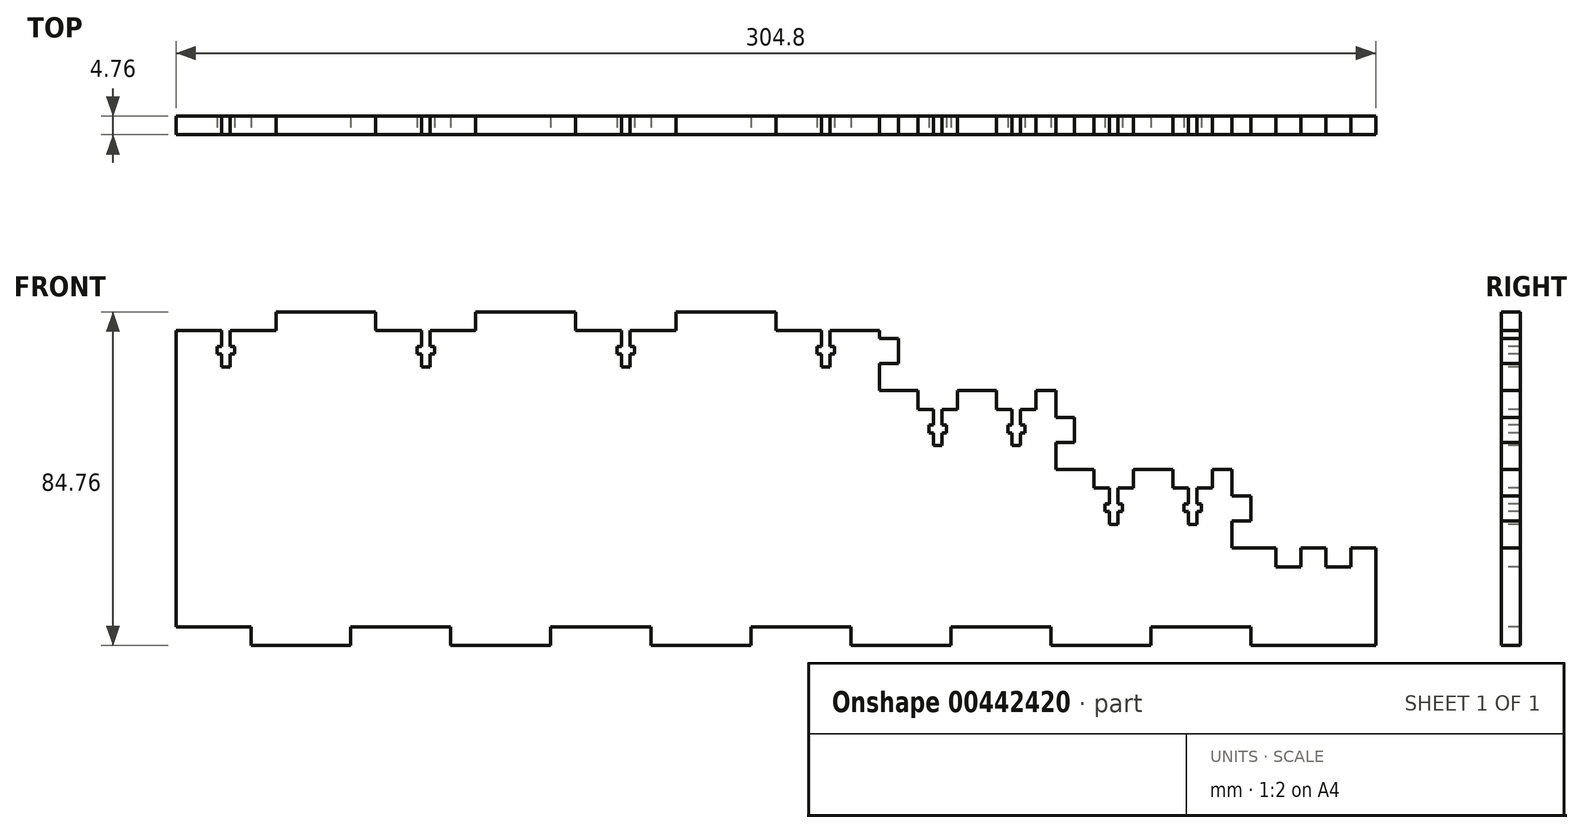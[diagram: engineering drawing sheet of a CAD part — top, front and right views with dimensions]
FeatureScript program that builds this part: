
annotation { "Feature Type Name" : "Feature", "Feature Type Description" : "" }
export const myFeature = defineFeature(function(context is Context, id is Id, definition is map)
    precondition{}
    {
        {
            var Q0;
            Q0=qCreatedBy(makeId("Front.planeOp"),FACE);
            var sketch = newSketch(context, id + "F0", { "sketchPlane" : qUnion([Q0])});
            skLineSegment(sketch, "E0", {"start": v(0, 0) * mm, "end": v(-273.05, 0) * mm});
            skLineSegment(sketch, "E1", {"start": v(0, 0) * mm, "end": v(0, 44.76) * mm});
            skLineSegment(sketch, "E2", {"start": v(0, 44.76) * mm, "end": v(-44.76, 44.76) * mm});
            skLineSegment(sketch, "E3", {"start": v(-44.76, 44.76) * mm, "end": v(-44.76, 64.76) * mm});
            skLineSegment(sketch, "E4", {"start": v(-44.76, 64.76) * mm, "end": v(-89.53, 64.76) * mm});
            skLineSegment(sketch, "E5", {"start": v(-89.53, 64.76) * mm, "end": v(-89.53, 84.76) * mm});
            skLineSegment(sketch, "E6", {"start": v(-89.53, 84.76) * mm, "end": v(-129.53, 84.76) * mm});
            skLineSegment(sketch, "E7", {"start": v(-129.53, 84.76) * mm, "end": v(-129.53, 84.76) * mm});
            skLineSegment(sketch, "E8", {"start": v(-273.05, 0) * mm, "end": v(-273.05, 84.76) * mm});
            skLineSegment(sketch, "E9", {"start": v(-273.05, 84.76) * mm, "end": v(-129.53, 84.76) * mm});
            skSolve(sketch);
        }
        {
            var Q0;
            Q0 = qSketchRegion(id + "F0", true);
            extrude(context, id + "F1", {"entities" : qUnion([Q0]), "depth" : 4.76 * mm});
        }
        {
            var Q0;
            Q0=makeQuery(id+"F1.opExtrude","CAP_FACE",FACE,{"disambiguationData":[OSD([sQuery(id+"F0.wireOp",EDGE,"E0"),sQuery(id+"F0.wireOp",EDGE,"E1"),sQuery(id+"F0.wireOp",EDGE,"E2"),sQuery(id+"F0.wireOp",EDGE,"E3"),sQuery(id+"F0.wireOp",EDGE,"E4"),sQuery(id+"F0.wireOp",EDGE,"E5"),sQuery(id+"F0.wireOp",EDGE,"xr6CjHdG-dKha-QLbm-3Mmw-o4ug5BnT2X88"),sQuery(id+"F0.wireOp",EDGE,"KsieTqkb-OR1U-vuQU-pcSh-D3RKZmKvM4ye")])],"isStart":false});
            var sketch = newSketch(context, id + "F2", { "sketchPlane" : qUnion([Q0])});
            skLineSegment(sketch, "E10", {"start": v(-254, 0) * mm, "end": v(-254, 4.76) * mm});
            skLineSegment(sketch, "E11.1.0.0", {"start": v(-228.6, 0) * mm, "end": v(-228.6, 4.76) * mm});
            skLineSegment(sketch, "E11.2.0.0", {"start": v(-203.2, 0) * mm, "end": v(-203.2, 4.76) * mm});
            skLineSegment(sketch, "E11.3.0.0", {"start": v(-177.8, 0) * mm, "end": v(-177.8, 4.76) * mm});
            skLineSegment(sketch, "E11.4.0.0", {"start": v(-152.4, 0) * mm, "end": v(-152.4, 4.76) * mm});
            skLineSegment(sketch, "E11.5.0.0", {"start": v(-127, 0) * mm, "end": v(-127, 4.76) * mm});
            skLineSegment(sketch, "E11.6.0.0", {"start": v(-101.6, 0) * mm, "end": v(-101.6, 4.76) * mm});
            skLineSegment(sketch, "E11.7.0.0", {"start": v(-76.2, 0) * mm, "end": v(-76.2, 4.76) * mm});
            skLineSegment(sketch, "E11.8.0.0", {"start": v(-50.8, 0) * mm, "end": v(-50.8, 4.76) * mm});
            skLineSegment(sketch, "E11.9.0.0", {"start": v(-25.4, 0) * mm, "end": v(-25.4, 4.76) * mm});
            skLineSegment(sketch, "E11.direction1", {"start": v(-254, 0) * mm, "end": v(-228.6, 0) * mm, "construction": true});
            skLineSegment(sketch, "E12", {"start": v(0, 4.76) * mm, "end": v(0, 0) * mm});
            skLineSegment(sketch, "E13", {"start": v(-254, 0) * mm, "end": v(0, 0) * mm});
            skLineSegment(sketch, "E14", {"start": v(-228.6, 4.76) * mm, "end": v(-203.2, 4.76) * mm});
            skLineSegment(sketch, "E15", {"start": v(-203.2, 0) * mm, "end": v(-228.6, 0) * mm});
            skLineSegment(sketch, "E16", {"start": v(-177.8, 4.76) * mm, "end": v(-152.4, 4.76) * mm});
            skLineSegment(sketch, "E17", {"start": v(-177.8, 0) * mm, "end": v(-152.4, 0) * mm});
            skLineSegment(sketch, "E18", {"start": v(-127, 4.76) * mm, "end": v(-101.6, 4.76) * mm});
            skLineSegment(sketch, "E19", {"start": v(-101.6, 0) * mm, "end": v(-127, 0) * mm});
            skLineSegment(sketch, "E20", {"start": v(-76.2, 4.76) * mm, "end": v(-50.8, 4.76) * mm});
            skLineSegment(sketch, "E21", {"start": v(-50.8, 0) * mm, "end": v(-76.2, 0) * mm});
            skLineSegment(sketch, "E22", {"start": v(-25.4, 4.76) * mm, "end": v(0, 4.76) * mm});
            skLineSegment(sketch, "E23", {"start": v(0, 0) * mm, "end": v(-25.4, 0) * mm});
            skLineSegment(sketch, "E24", {"start": v(-254, 4.76) * mm, "end": v(-273.05, 4.76) * mm});
            skLineSegment(sketch, "E25", {"start": v(-273.05, 4.76) * mm, "end": v(-273.05, 0) * mm});
            skLineSegment(sketch, "E26", {"start": v(-273.05, 0) * mm, "end": v(-254, 0) * mm});
            skSolve(sketch);
        }
        {
            var Q0;
            Q0 = qSketchRegion(id + "F2", true);
            extrude(context, id + "F3", {"entities" : qUnion([Q0]), "operationType" : NewBodyOperationType.REMOVE, "oppositeDirection" : true, "depth" : 25.4 * mm});
        }
        {
            var Q0;
            Q0=makeQuery(id+"F1.opExtrude","CAP_FACE",FACE,{"disambiguationData":[OSD([sQuery(id+"F0.wireOp",EDGE,"E0"),sQuery(id+"F0.wireOp",EDGE,"E1"),sQuery(id+"F0.wireOp",EDGE,"E2"),sQuery(id+"F0.wireOp",EDGE,"E3"),sQuery(id+"F0.wireOp",EDGE,"E4"),sQuery(id+"F0.wireOp",EDGE,"E5"),sQuery(id+"F0.wireOp",EDGE,"E6"),sQuery(id+"F0.wireOp",EDGE,"E7"),sQuery(id+"F0.wireOp",EDGE,"E8"),sQuery(id+"F0.wireOp",EDGE,"E9")])],"isStart":false});
            var sketch = newSketch(context, id + "F4", { "sketchPlane" : qUnion([Q0])});
            skLineSegment(sketch, "E27", {"start": v(-44.76, 54.76) * mm, "end": v(-80.66, 54.76) * mm, "construction": true});
            skLineSegment(sketch, "E28.bottom", {"start": v(-49.53, 57.94) * mm, "end": v(-44.76, 57.94) * mm});
            skLineSegment(sketch, "E28.top", {"start": v(-45, 51.59) * mm, "end": v(-44.76, 51.59) * mm});
            skLineSegment(sketch, "E29", {"start": v(-49.53, 57.94) * mm, "end": v(-49.53, 64.76) * mm});
            skLineSegment(sketch, "E30", {"start": v(-49.53, 64.76) * mm, "end": v(-44.76, 64.76) * mm});
            skLineSegment(sketch, "E31", {"start": v(-44.76, 64.76) * mm, "end": v(-44.76, 57.94) * mm});
            skLineSegment(sketch, "E32", {"start": v(-45, 51.59) * mm, "end": v(-45, 44.76) * mm});
            skLineSegment(sketch, "E33", {"start": v(-45, 44.76) * mm, "end": v(-44.76, 44.76) * mm});
            skLineSegment(sketch, "E34", {"start": v(-44.76, 44.76) * mm, "end": v(-44.76, 51.59) * mm});
            skLineSegment(sketch, "E35", {"start": v(-45, 51.59) * mm, "end": v(-49.53, 51.59) * mm});
            skLineSegment(sketch, "E36", {"start": v(-49.53, 51.59) * mm, "end": v(-49.53, 44.76) * mm});
            skLineSegment(sketch, "E37", {"start": v(-49.53, 44.76) * mm, "end": v(-45, 44.76) * mm});
            skLineSegment(sketch, "E38", {"start": v(-89.53, 74.76) * mm, "end": v(-114.43, 74.76) * mm, "construction": true});
            skLineSegment(sketch, "E39.bottom", {"start": v(-94.29, 77.94) * mm, "end": v(-89.53, 77.94) * mm});
            skLineSegment(sketch, "E39.top", {"start": v(-94.29, 71.59) * mm, "end": v(-89.53, 71.59) * mm});
            skLineSegment(sketch, "E40", {"start": v(-94.29, 77.94) * mm, "end": v(-94.29, 84.76) * mm});
            skLineSegment(sketch, "E41", {"start": v(-94.29, 84.76) * mm, "end": v(-89.53, 84.76) * mm});
            skLineSegment(sketch, "E42", {"start": v(-89.53, 84.76) * mm, "end": v(-89.53, 77.94) * mm});
            skLineSegment(sketch, "E43", {"start": v(-89.53, 71.59) * mm, "end": v(-89.53, 64.76) * mm});
            skLineSegment(sketch, "E44", {"start": v(-89.53, 64.76) * mm, "end": v(-94.29, 64.76) * mm});
            skLineSegment(sketch, "E45", {"start": v(-94.29, 64.76) * mm, "end": v(-94.29, 71.59) * mm});
            skSolve(sketch);
        }
        {
            var Q0;
            Q0 = qSketchRegion(id + "F4", true);
            extrude(context, id + "F5", {"entities" : qUnion([Q0]), "operationType" : NewBodyOperationType.REMOVE, "oppositeDirection" : true, "depth" : 25.4 * mm});
        }
        {
            var Q0;
            Q0=makeQuery(id+"F1.opExtrude","CAP_FACE",FACE,{"disambiguationData":[OSD([sQuery(id+"F0.wireOp",EDGE,"E0"),sQuery(id+"F0.wireOp",EDGE,"E1"),sQuery(id+"F0.wireOp",EDGE,"E2"),sQuery(id+"F0.wireOp",EDGE,"E3"),sQuery(id+"F0.wireOp",EDGE,"E4"),sQuery(id+"F0.wireOp",EDGE,"E5"),sQuery(id+"F0.wireOp",EDGE,"E6"),sQuery(id+"F0.wireOp",EDGE,"E8"),sQuery(id+"F0.wireOp",EDGE,"E9")])],"isStart":false});
            var sketch = newSketch(context, id + "F6", { "sketchPlane" : qUnion([Q0])});
            skLineSegment(sketch, "E46", {"start": v(0, 44.76) * mm, "end": v(0, 24.76) * mm});
            skLineSegment(sketch, "E47", {"start": v(0, 24.76) * mm, "end": v(31.75, 24.76) * mm});
            skLineSegment(sketch, "E48", {"start": v(31.75, 24.76) * mm, "end": v(31.75, 0) * mm});
            skLineSegment(sketch, "E49", {"start": v(31.75, 0) * mm, "end": v(0, 0) * mm});
            skLineSegment(sketch, "E50", {"start": v(0, 0) * mm, "end": v(0, 24.76) * mm});
            skSolve(sketch);
        }
        {
            var Q0;
            Q0 = qSketchRegion(id + "F6", true);
            extrude(context, id + "F7", {"entities" : qUnion([Q0]), "operationType" : NewBodyOperationType.ADD, "oppositeDirection" : true, "depth" : 4.76 * mm});
        }
        {
            var Q0;
            Q0=makeQuery(id+"F7.boolean.opBoolean","MERGE",FACE,{"derivedFrom":[makeQuery(id+"F1.opExtrude","CAP_FACE",FACE,{"disambiguationData":[OSD([sQuery(id+"F0.wireOp",EDGE,"E0"),sQuery(id+"F0.wireOp",EDGE,"E1"),sQuery(id+"F0.wireOp",EDGE,"E2"),sQuery(id+"F0.wireOp",EDGE,"E3"),sQuery(id+"F0.wireOp",EDGE,"E4"),sQuery(id+"F0.wireOp",EDGE,"E5"),sQuery(id+"F0.wireOp",EDGE,"E6"),sQuery(id+"F0.wireOp",EDGE,"E8"),sQuery(id+"F0.wireOp",EDGE,"E9")])],"isStart":false}),makeQuery(id+"F7.opExtrude","CAP_FACE",FACE,{"disambiguationData":[OSD([sQuery(id+"F6.wireOp",EDGE,"E47"),sQuery(id+"F6.wireOp",EDGE,"E48"),sQuery(id+"F6.wireOp",EDGE,"E49"),sQuery(id+"F6.wireOp",EDGE,"E50")])],"isStart":true})]});
            var sketch = newSketch(context, id + "F8", { "sketchPlane" : qUnion([Q0])});
            skLineSegment(sketch, "E51", {"start": v(0, 34.76) * mm, "end": v(13.92, 34.76) * mm, "construction": true});
            skLineSegment(sketch, "E52", {"start": v(0, 37.94) * mm, "end": v(10.62, 37.94) * mm, "construction": true});
            skLineSegment(sketch, "E53", {"start": v(0, 37.94) * mm, "end": v(0, 44.76) * mm});
            skLineSegment(sketch, "E54", {"start": v(0, 44.76) * mm, "end": v(-4.76, 44.76) * mm});
            skLineSegment(sketch, "E55", {"start": v(-4.76, 44.76) * mm, "end": v(-4.76, 37.94) * mm});
            skLineSegment(sketch, "E56", {"start": v(-4.76, 37.94) * mm, "end": v(0, 37.94) * mm});
            skLineSegment(sketch, "E57.MirrorCS", {"start": v(0, 24.76) * mm, "end": v(-4.76, 24.76) * mm});
            skLineSegment(sketch, "E58.MirrorCS", {"start": v(-4.76, 24.76) * mm, "end": v(-4.76, 31.59) * mm});
            skLineSegment(sketch, "E59.MirrorCS", {"start": v(0, 31.59) * mm, "end": v(0, 24.76) * mm});
            skLineSegment(sketch, "E60.MirrorCS", {"start": v(-4.76, 31.59) * mm, "end": v(0, 31.59) * mm});
            skSolve(sketch);
        }
        {
            var Q0;
            Q0 = qSketchRegion(id + "F8", true);
            extrude(context, id + "F9", {"entities" : qUnion([Q0]), "operationType" : NewBodyOperationType.REMOVE, "oppositeDirection" : true, "depth" : 25.4 * mm});
        }
        {
            var Q0;
            Q0=makeQuery(id+"F7.boolean.opBoolean","MERGE",FACE,{"derivedFrom":[makeQuery(id+"F1.opExtrude","CAP_FACE",FACE,{"disambiguationData":[OSD([sQuery(id+"F0.wireOp",EDGE,"E0"),sQuery(id+"F0.wireOp",EDGE,"E1"),sQuery(id+"F0.wireOp",EDGE,"E2"),sQuery(id+"F0.wireOp",EDGE,"E3"),sQuery(id+"F0.wireOp",EDGE,"E4"),sQuery(id+"F0.wireOp",EDGE,"E5"),sQuery(id+"F0.wireOp",EDGE,"E6"),sQuery(id+"F0.wireOp",EDGE,"E8"),sQuery(id+"F0.wireOp",EDGE,"E9")])],"isStart":false}),makeQuery(id+"F7.opExtrude","CAP_FACE",FACE,{"disambiguationData":[OSD([sQuery(id+"F6.wireOp",EDGE,"E47"),sQuery(id+"F6.wireOp",EDGE,"E48"),sQuery(id+"F6.wireOp",EDGE,"E49"),sQuery(id+"F6.wireOp",EDGE,"E50")])],"isStart":true})]});
            var sketch = newSketch(context, id + "F10", { "sketchPlane" : qUnion([Q0])});
            skLineSegment(sketch, "E61", {"start": v(0, 31.59) * mm, "end": v(0, 24.76) * mm, "construction": true});
            skLineSegment(sketch, "E62", {"start": v(6.35, 24.76) * mm, "end": v(6.35, 20) * mm});
            skLineSegment(sketch, "E63", {"start": v(6.35, 20) * mm, "end": v(12.7, 20) * mm});
            skLineSegment(sketch, "E64", {"start": v(12.7, 20) * mm, "end": v(12.7, 24.76) * mm});
            skLineSegment(sketch, "E65", {"start": v(6.35, 24.76) * mm, "end": v(12.7, 24.76) * mm});
            skLineSegment(sketch, "E66.1.0.0", {"start": v(19.05, 24.76) * mm, "end": v(19.05, 20) * mm});
            skLineSegment(sketch, "E66.1.0.1", {"start": v(19.05, 24.76) * mm, "end": v(25.4, 24.76) * mm});
            skLineSegment(sketch, "E66.1.0.2", {"start": v(25.4, 20) * mm, "end": v(25.4, 24.76) * mm});
            skLineSegment(sketch, "E66.1.0.3", {"start": v(19.05, 20) * mm, "end": v(25.4, 20) * mm});
            skLineSegment(sketch, "E66.direction1", {"start": v(6.35, 20) * mm, "end": v(19.05, 20) * mm, "construction": true});
            skSolve(sketch);
        }
        {
            var Q0;
            Q0 = qSketchRegion(id + "F10", true);
            extrude(context, id + "F11", {"entities" : qUnion([Q0]), "operationType" : NewBodyOperationType.REMOVE, "oppositeDirection" : true, "depth" : 25.4 * mm});
        }
        {
            var Q0;
            Q0=makeQuery(id+"F7.boolean.opBoolean","MERGE",FACE,{"derivedFrom":[makeQuery(id+"F1.opExtrude","CAP_FACE",FACE,{"disambiguationData":[OSD([sQuery(id+"F0.wireOp",EDGE,"E0"),sQuery(id+"F0.wireOp",EDGE,"E1"),sQuery(id+"F0.wireOp",EDGE,"E2"),sQuery(id+"F0.wireOp",EDGE,"E3"),sQuery(id+"F0.wireOp",EDGE,"E4"),sQuery(id+"F0.wireOp",EDGE,"E5"),sQuery(id+"F0.wireOp",EDGE,"E6"),sQuery(id+"F0.wireOp",EDGE,"E8"),sQuery(id+"F0.wireOp",EDGE,"E9")])],"isStart":false}),makeQuery(id+"F7.opExtrude","CAP_FACE",FACE,{"disambiguationData":[OSD([sQuery(id+"F6.wireOp",EDGE,"E47"),sQuery(id+"F6.wireOp",EDGE,"E48"),sQuery(id+"F6.wireOp",EDGE,"E49"),sQuery(id+"F6.wireOp",EDGE,"E50")])],"isStart":true})]});
            var sketch = newSketch(context, id + "F12", { "sketchPlane" : qUnion([Q0])});
            skLineSegment(sketch, "E67", {"start": v(-44.76, 51.59) * mm, "end": v(-44.76, 44.76) * mm, "construction": true});
            skLineSegment(sketch, "E68", {"start": v(-29.76, 44.76) * mm, "end": v(-29.76, 40) * mm});
            skLineSegment(sketch, "E69", {"start": v(-39.76, 40) * mm, "end": v(-29.76, 40) * mm});
            skLineSegment(sketch, "E70", {"start": v(-39.76, 40) * mm, "end": v(-39.76, 44.76) * mm});
            skLineSegment(sketch, "E71", {"start": v(-29.76, 44.76) * mm, "end": v(-39.76, 44.76) * mm});
            skLineSegment(sketch, "E72", {"start": v(-34.76, 44.76) * mm, "end": v(-34.76, 40) * mm, "construction": true});
            skLineSegment(sketch, "E73", {"start": v(-4.76, 44.76) * mm, "end": v(-4.76, 51.59) * mm, "construction": true});
            skLineSegment(sketch, "E74", {"start": v(-4.76, 51.59) * mm, "end": v(-44.76, 51.59) * mm, "construction": true});
            skLineSegment(sketch, "E75", {"start": v(-24.76, 51.59) * mm, "end": v(-24.76, 44.76) * mm, "construction": true});
            skLineSegment(sketch, "E76.MirrorCS", {"start": v(-19.76, 44.76) * mm, "end": v(-9.76, 44.76) * mm});
            skLineSegment(sketch, "E77.MirrorCS", {"start": v(-9.76, 40) * mm, "end": v(-9.76, 44.76) * mm});
            skLineSegment(sketch, "E78.MirrorCS", {"start": v(-9.76, 40) * mm, "end": v(-19.76, 40) * mm});
            skLineSegment(sketch, "E79.MirrorCS", {"start": v(-19.76, 44.76) * mm, "end": v(-19.76, 40) * mm});
            skLineSegment(sketch, "E80", {"start": v(-89.53, 71.59) * mm, "end": v(-89.53, 64.76) * mm, "construction": true});
            skLineSegment(sketch, "E81", {"start": v(-89.53, 71.59) * mm, "end": v(-49.53, 71.59) * mm, "construction": true});
            skLineSegment(sketch, "E82", {"start": v(-49.53, 71.59) * mm, "end": v(-49.53, 64.76) * mm, "construction": true});
            skLineSegment(sketch, "E83", {"start": v(-69.53, 71.59) * mm, "end": v(-69.53, 64.76) * mm, "construction": true});
            skLineSegment(sketch, "E84", {"start": v(-84.53, 64.76) * mm, "end": v(-84.53, 60) * mm});
            skLineSegment(sketch, "E85", {"start": v(-84.53, 60) * mm, "end": v(-74.52, 60) * mm});
            skLineSegment(sketch, "E86", {"start": v(-74.53, 60) * mm, "end": v(-74.53, 64.76) * mm});
            skLineSegment(sketch, "E87", {"start": v(-74.53, 64.76) * mm, "end": v(-84.53, 64.76) * mm});
            skLineSegment(sketch, "E88", {"start": v(-79.52, 64.76) * mm, "end": v(-79.52, 60) * mm, "construction": true});
            skLineSegment(sketch, "E89.MirrorCS", {"start": v(-64.52, 64.76) * mm, "end": v(-54.53, 64.76) * mm});
            skLineSegment(sketch, "E90.MirrorCS", {"start": v(-54.53, 64.76) * mm, "end": v(-54.53, 60) * mm});
            skLineSegment(sketch, "E91.MirrorCS", {"start": v(-54.53, 60) * mm, "end": v(-64.53, 60) * mm});
            skLineSegment(sketch, "E92.MirrorCS", {"start": v(-64.53, 60) * mm, "end": v(-64.53, 64.76) * mm});
            skSolve(sketch);
        }
        {
            var Q0;
            Q0 = qSketchRegion(id + "F12", true);
            extrude(context, id + "F13", {"entities" : qUnion([Q0]), "operationType" : NewBodyOperationType.REMOVE, "oppositeDirection" : true, "depth" : 25.4 * mm});
        }
        {
            var Q0;
            Q0=makeQuery(id+"F7.boolean.opBoolean","MERGE",FACE,{"derivedFrom":[makeQuery(id+"F1.opExtrude","CAP_FACE",FACE,{"disambiguationData":[OSD([sQuery(id+"F0.wireOp",EDGE,"E0"),sQuery(id+"F0.wireOp",EDGE,"E1"),sQuery(id+"F0.wireOp",EDGE,"E2"),sQuery(id+"F0.wireOp",EDGE,"E3"),sQuery(id+"F0.wireOp",EDGE,"E4"),sQuery(id+"F0.wireOp",EDGE,"E5"),sQuery(id+"F0.wireOp",EDGE,"E6"),sQuery(id+"F0.wireOp",EDGE,"E8"),sQuery(id+"F0.wireOp",EDGE,"E9")])],"isStart":false}),makeQuery(id+"F7.opExtrude","CAP_FACE",FACE,{"disambiguationData":[OSD([sQuery(id+"F6.wireOp",EDGE,"E47"),sQuery(id+"F6.wireOp",EDGE,"E48"),sQuery(id+"F6.wireOp",EDGE,"E49"),sQuery(id+"F6.wireOp",EDGE,"E50")])],"isStart":true})]});
            var sketch = newSketch(context, id + "F14", { "sketchPlane" : qUnion([Q0])});
            skLineSegment(sketch, "E93", {"start": v(-247.65, 84.76) * mm, "end": v(-247.65, 80) * mm});
            skLineSegment(sketch, "E94", {"start": v(-222.25, 80) * mm, "end": v(-222.25, 84.76) * mm});
            skLineSegment(sketch, "E95", {"start": v(-222.25, 84.76) * mm, "end": v(-247.65, 84.76) * mm});
            skLineSegment(sketch, "E96.1.0.0", {"start": v(-196.85, 84.76) * mm, "end": v(-196.85, 80) * mm});
            skLineSegment(sketch, "E96.1.0.3", {"start": v(-171.45, 80) * mm, "end": v(-171.45, 84.76) * mm});
            skLineSegment(sketch, "E96.2.0.0", {"start": v(-146.05, 84.76) * mm, "end": v(-146.05, 80) * mm});
            skLineSegment(sketch, "E96.2.0.3", {"start": v(-120.65, 80) * mm, "end": v(-120.65, 84.76) * mm});
            skLineSegment(sketch, "E96.direction1", {"start": v(-222.25, 80) * mm, "end": v(-196.85, 80) * mm, "construction": true});
            skLineSegment(sketch, "E97", {"start": v(-247.65, 80) * mm, "end": v(-273.05, 80) * mm});
            skLineSegment(sketch, "E98", {"start": v(-273.05, 80) * mm, "end": v(-273.05, 84.76) * mm});
            skLineSegment(sketch, "E99", {"start": v(-273.05, 84.76) * mm, "end": v(-247.65, 84.76) * mm});
            skLineSegment(sketch, "E100", {"start": v(-222.25, 84.76) * mm, "end": v(-196.85, 84.76) * mm});
            skLineSegment(sketch, "E101", {"start": v(-222.25, 80) * mm, "end": v(-196.85, 80) * mm});
            skLineSegment(sketch, "E102", {"start": v(-171.45, 84.76) * mm, "end": v(-146.05, 84.76) * mm});
            skLineSegment(sketch, "E103", {"start": v(-146.05, 80) * mm, "end": v(-171.45, 80) * mm});
            skLineSegment(sketch, "E104", {"start": v(-120.65, 84.76) * mm, "end": v(-94.29, 84.76) * mm});
            skLineSegment(sketch, "E105", {"start": v(-120.65, 80) * mm, "end": v(-94.29, 80) * mm});
            skLineSegment(sketch, "E106", {"start": v(-94.29, 80) * mm, "end": v(-94.29, 84.76) * mm});
            skSolve(sketch);
        }
        {
            var Q0;
            Q0 = qSketchRegion(id + "F14", true);
            extrude(context, id + "F15", {"entities" : qUnion([Q0]), "operationType" : NewBodyOperationType.REMOVE, "oppositeDirection" : true, "depth" : 25.4 * mm});
        }
        {
            var Q0;
            Q0=makeQuery(id+"F7.boolean.opBoolean","MERGE",FACE,{"derivedFrom":[makeQuery(id+"F1.opExtrude","CAP_FACE",FACE,{"disambiguationData":[OSD([sQuery(id+"F0.wireOp",EDGE,"E0"),sQuery(id+"F0.wireOp",EDGE,"E1"),sQuery(id+"F0.wireOp",EDGE,"E2"),sQuery(id+"F0.wireOp",EDGE,"E3"),sQuery(id+"F0.wireOp",EDGE,"E4"),sQuery(id+"F0.wireOp",EDGE,"E5"),sQuery(id+"F0.wireOp",EDGE,"E6"),sQuery(id+"F0.wireOp",EDGE,"E8"),sQuery(id+"F0.wireOp",EDGE,"E9")])],"isStart":false}),makeQuery(id+"F7.opExtrude","CAP_FACE",FACE,{"disambiguationData":[OSD([sQuery(id+"F6.wireOp",EDGE,"E47"),sQuery(id+"F6.wireOp",EDGE,"E48"),sQuery(id+"F6.wireOp",EDGE,"E49"),sQuery(id+"F6.wireOp",EDGE,"E50")])],"isStart":true})]});
            var sketch = newSketch(context, id + "F16", { "sketchPlane" : qUnion([Q0])});
            skLineSegment(sketch, "E107", {"start": v(-34.76, 40) * mm, "end": v(-34.76, 31.6) * mm, "construction": true});
            skLineSegment(sketch, "E108", {"start": v(-14.76, 40) * mm, "end": v(-14.76, 29.64) * mm, "construction": true});
            skLineSegment(sketch, "E109", {"start": v(-59.53, 60) * mm, "end": v(-59.53, 51.2) * mm, "construction": true});
            skPoint(sketch, "E109.endSnap0", {"position": v(-59.53, 60) * mm});
            skLineSegment(sketch, "E110", {"start": v(-79.52, 60) * mm, "end": v(-79.52, 51.39) * mm, "construction": true});
            skLineSegment(sketch, "E111", {"start": v(-35.86, 40) * mm, "end": v(-35.86, 36) * mm});
            skLineSegment(sketch, "E112", {"start": v(-35.86, 36) * mm, "end": v(-36.96, 36) * mm});
            skLineSegment(sketch, "E113", {"start": v(-36.96, 36) * mm, "end": v(-36.96, 34) * mm});
            skLineSegment(sketch, "E114", {"start": v(-36.96, 34) * mm, "end": v(-35.86, 34) * mm});
            skLineSegment(sketch, "E115", {"start": v(-35.86, 34) * mm, "end": v(-35.86, 30.76) * mm});
            skLineSegment(sketch, "E116", {"start": v(-35.86, 30.76) * mm, "end": v(-34.76, 30.76) * mm});
            skPoint(sketch, "E117.orphan", {"position": v(-39.76, 36) * mm});
            skLineSegment(sketch, "E118.MirrorCS", {"start": v(-33.66, 40) * mm, "end": v(-33.66, 36) * mm});
            skLineSegment(sketch, "E119.MirrorCS", {"start": v(-33.66, 36) * mm, "end": v(-32.56, 36) * mm});
            skLineSegment(sketch, "E120.MirrorCS", {"start": v(-32.56, 36) * mm, "end": v(-32.56, 34) * mm});
            skLineSegment(sketch, "E121.MirrorCS", {"start": v(-32.56, 34) * mm, "end": v(-33.66, 34) * mm});
            skLineSegment(sketch, "E122.MirrorCS", {"start": v(-33.66, 34) * mm, "end": v(-33.66, 30.76) * mm});
            skLineSegment(sketch, "E123.MirrorCS", {"start": v(-33.66, 30.76) * mm, "end": v(-34.76, 30.76) * mm});
            skLineSegment(sketch, "E124", {"start": v(-35.86, 40) * mm, "end": v(-33.66, 40) * mm});
            skLineSegment(sketch, "E125", {"start": v(-15.86, 40) * mm, "end": v(-15.86, 36) * mm});
            skLineSegment(sketch, "E126", {"start": v(-15.86, 36) * mm, "end": v(-16.96, 36) * mm});
            skLineSegment(sketch, "E127", {"start": v(-16.96, 36) * mm, "end": v(-16.96, 34) * mm});
            skLineSegment(sketch, "E128", {"start": v(-16.96, 34) * mm, "end": v(-15.86, 34) * mm});
            skLineSegment(sketch, "E129", {"start": v(-15.86, 34) * mm, "end": v(-15.86, 30.76) * mm});
            skLineSegment(sketch, "E130", {"start": v(-15.86, 30.76) * mm, "end": v(-14.76, 30.76) * mm});
            skLineSegment(sketch, "E131.MirrorCS", {"start": v(-13.66, 40) * mm, "end": v(-13.66, 36) * mm});
            skLineSegment(sketch, "E132.MirrorCS", {"start": v(-13.66, 36) * mm, "end": v(-12.56, 36) * mm});
            skLineSegment(sketch, "E133.MirrorCS", {"start": v(-12.56, 36) * mm, "end": v(-12.56, 34) * mm});
            skLineSegment(sketch, "E134.MirrorCS", {"start": v(-12.56, 34) * mm, "end": v(-13.66, 34) * mm});
            skLineSegment(sketch, "E135.MirrorCS", {"start": v(-13.66, 34) * mm, "end": v(-13.66, 30.76) * mm});
            skLineSegment(sketch, "E136.MirrorCS", {"start": v(-13.66, 30.76) * mm, "end": v(-14.76, 30.76) * mm});
            skLineSegment(sketch, "E137", {"start": v(-15.86, 40) * mm, "end": v(-13.66, 40) * mm});
            skLineSegment(sketch, "E138", {"start": v(-80.62, 60) * mm, "end": v(-80.62, 56) * mm});
            skLineSegment(sketch, "E139", {"start": v(-80.62, 56) * mm, "end": v(-81.72, 56) * mm});
            skLineSegment(sketch, "E140", {"start": v(-81.72, 56) * mm, "end": v(-81.72, 54) * mm});
            skLineSegment(sketch, "E141", {"start": v(-81.72, 54) * mm, "end": v(-80.62, 54) * mm});
            skLineSegment(sketch, "E142", {"start": v(-80.62, 54) * mm, "end": v(-80.62, 50.76) * mm});
            skLineSegment(sketch, "E143", {"start": v(-80.62, 50.76) * mm, "end": v(-79.52, 50.76) * mm});
            skLineSegment(sketch, "E144.MirrorCS", {"start": v(-78.42, 60) * mm, "end": v(-78.42, 56) * mm});
            skLineSegment(sketch, "E145.MirrorCS", {"start": v(-78.42, 56) * mm, "end": v(-77.32, 56) * mm});
            skLineSegment(sketch, "E146.MirrorCS", {"start": v(-77.32, 56) * mm, "end": v(-77.32, 54) * mm});
            skLineSegment(sketch, "E147.MirrorCS", {"start": v(-77.32, 54) * mm, "end": v(-78.42, 54) * mm});
            skLineSegment(sketch, "E148.MirrorCS", {"start": v(-78.42, 54) * mm, "end": v(-78.42, 50.76) * mm});
            skLineSegment(sketch, "E149.MirrorCS", {"start": v(-78.42, 50.76) * mm, "end": v(-79.52, 50.76) * mm});
            skLineSegment(sketch, "E150", {"start": v(-80.62, 60) * mm, "end": v(-78.42, 60) * mm});
            skLineSegment(sketch, "E151", {"start": v(-60.63, 60) * mm, "end": v(-60.63, 56) * mm});
            skLineSegment(sketch, "E152", {"start": v(-60.63, 56) * mm, "end": v(-61.73, 56) * mm});
            skLineSegment(sketch, "E153", {"start": v(-61.73, 56) * mm, "end": v(-61.73, 54) * mm});
            skLineSegment(sketch, "E154", {"start": v(-61.73, 54) * mm, "end": v(-60.63, 54) * mm});
            skLineSegment(sketch, "E155", {"start": v(-60.63, 54) * mm, "end": v(-60.63, 50.76) * mm});
            skLineSegment(sketch, "E156", {"start": v(-60.63, 50.76) * mm, "end": v(-59.53, 50.76) * mm});
            skLineSegment(sketch, "E157.MirrorCS", {"start": v(-58.43, 60) * mm, "end": v(-58.43, 56) * mm});
            skLineSegment(sketch, "E158.MirrorCS", {"start": v(-58.43, 56) * mm, "end": v(-57.33, 56) * mm});
            skLineSegment(sketch, "E159.MirrorCS", {"start": v(-57.33, 56) * mm, "end": v(-57.33, 54) * mm});
            skLineSegment(sketch, "E160.MirrorCS", {"start": v(-57.33, 54) * mm, "end": v(-58.43, 54) * mm});
            skLineSegment(sketch, "E161.MirrorCS", {"start": v(-58.43, 54) * mm, "end": v(-58.43, 50.76) * mm});
            skLineSegment(sketch, "E162.MirrorCS", {"start": v(-58.43, 50.76) * mm, "end": v(-59.53, 50.76) * mm});
            skLineSegment(sketch, "E163", {"start": v(-60.63, 60) * mm, "end": v(-58.43, 60) * mm});
            skLineSegment(sketch, "E164", {"start": v(-260.35, 80) * mm, "end": v(-260.35, 70.89) * mm, "construction": true});
            skLineSegment(sketch, "E165.1.0.0", {"start": v(-209.55, 80) * mm, "end": v(-209.55, 70.89) * mm, "construction": true});
            skLineSegment(sketch, "E165.2.0.0", {"start": v(-158.75, 80) * mm, "end": v(-158.75, 70.89) * mm, "construction": true});
            skLineSegment(sketch, "E165.3.0.0", {"start": v(-107.95, 80) * mm, "end": v(-107.95, 70.89) * mm, "construction": true});
            skLineSegment(sketch, "E165.direction1", {"start": v(-260.35, 70.89) * mm, "end": v(-209.55, 70.89) * mm, "construction": true});
            skLineSegment(sketch, "E166", {"start": v(-159.85, 80) * mm, "end": v(-159.85, 76) * mm});
            skLineSegment(sketch, "E167", {"start": v(-159.85, 76) * mm, "end": v(-160.95, 76) * mm});
            skLineSegment(sketch, "E168", {"start": v(-160.95, 76) * mm, "end": v(-160.95, 74) * mm});
            skLineSegment(sketch, "E169", {"start": v(-160.95, 74) * mm, "end": v(-159.85, 74) * mm});
            skLineSegment(sketch, "E170", {"start": v(-159.85, 74) * mm, "end": v(-159.85, 70.76) * mm});
            skLineSegment(sketch, "E171", {"start": v(-159.85, 70.76) * mm, "end": v(-158.75, 70.76) * mm});
            skLineSegment(sketch, "E172.MirrorCS", {"start": v(-157.65, 80) * mm, "end": v(-157.65, 76) * mm});
            skLineSegment(sketch, "E173.MirrorCS", {"start": v(-157.65, 76) * mm, "end": v(-156.55, 76) * mm});
            skLineSegment(sketch, "E174.MirrorCS", {"start": v(-156.55, 76) * mm, "end": v(-156.55, 74) * mm});
            skLineSegment(sketch, "E175.MirrorCS", {"start": v(-156.55, 74) * mm, "end": v(-157.65, 74) * mm});
            skLineSegment(sketch, "E176.MirrorCS", {"start": v(-157.65, 74) * mm, "end": v(-157.65, 70.76) * mm});
            skLineSegment(sketch, "E177.MirrorCS", {"start": v(-157.65, 70.76) * mm, "end": v(-158.75, 70.76) * mm});
            skLineSegment(sketch, "E178", {"start": v(-159.85, 80) * mm, "end": v(-157.65, 80) * mm});
            skLineSegment(sketch, "E179", {"start": v(-210.65, 80) * mm, "end": v(-210.65, 76) * mm});
            skLineSegment(sketch, "E180", {"start": v(-210.65, 76) * mm, "end": v(-211.75, 76) * mm});
            skLineSegment(sketch, "E181", {"start": v(-211.75, 76) * mm, "end": v(-211.75, 74) * mm});
            skLineSegment(sketch, "E182", {"start": v(-211.75, 74) * mm, "end": v(-210.65, 74) * mm});
            skLineSegment(sketch, "E183", {"start": v(-210.65, 74) * mm, "end": v(-210.65, 70.76) * mm});
            skLineSegment(sketch, "E184", {"start": v(-210.65, 70.76) * mm, "end": v(-209.55, 70.76) * mm});
            skLineSegment(sketch, "E185.MirrorCS", {"start": v(-208.45, 80) * mm, "end": v(-208.45, 76) * mm});
            skLineSegment(sketch, "E186.MirrorCS", {"start": v(-208.45, 76) * mm, "end": v(-207.35, 76) * mm});
            skLineSegment(sketch, "E187.MirrorCS", {"start": v(-207.35, 76) * mm, "end": v(-207.35, 74) * mm});
            skLineSegment(sketch, "E188.MirrorCS", {"start": v(-207.35, 74) * mm, "end": v(-208.45, 74) * mm});
            skLineSegment(sketch, "E189.MirrorCS", {"start": v(-208.45, 74) * mm, "end": v(-208.45, 70.76) * mm});
            skLineSegment(sketch, "E190.MirrorCS", {"start": v(-208.45, 70.76) * mm, "end": v(-209.55, 70.76) * mm});
            skLineSegment(sketch, "E191", {"start": v(-210.65, 80) * mm, "end": v(-208.45, 80) * mm});
            skLineSegment(sketch, "E192", {"start": v(-261.45, 80) * mm, "end": v(-261.45, 76) * mm});
            skLineSegment(sketch, "E193", {"start": v(-261.45, 76) * mm, "end": v(-262.55, 76) * mm});
            skLineSegment(sketch, "E194", {"start": v(-262.55, 76) * mm, "end": v(-262.55, 74) * mm});
            skLineSegment(sketch, "E195", {"start": v(-262.55, 74) * mm, "end": v(-261.45, 74) * mm});
            skLineSegment(sketch, "E196", {"start": v(-261.45, 74) * mm, "end": v(-261.45, 70.76) * mm});
            skLineSegment(sketch, "E197", {"start": v(-261.45, 70.76) * mm, "end": v(-260.35, 70.76) * mm});
            skLineSegment(sketch, "E198.MirrorCS", {"start": v(-259.25, 80) * mm, "end": v(-259.25, 76) * mm});
            skLineSegment(sketch, "E199.MirrorCS", {"start": v(-259.25, 76) * mm, "end": v(-258.15, 76) * mm});
            skLineSegment(sketch, "E200.MirrorCS", {"start": v(-258.15, 76) * mm, "end": v(-258.15, 74) * mm});
            skLineSegment(sketch, "E201.MirrorCS", {"start": v(-258.15, 74) * mm, "end": v(-259.25, 74) * mm});
            skLineSegment(sketch, "E202.MirrorCS", {"start": v(-259.25, 74) * mm, "end": v(-259.25, 70.76) * mm});
            skLineSegment(sketch, "E203.MirrorCS", {"start": v(-259.25, 70.76) * mm, "end": v(-260.35, 70.76) * mm});
            skLineSegment(sketch, "E204", {"start": v(-261.45, 80) * mm, "end": v(-259.25, 80) * mm});
            skLineSegment(sketch, "E205", {"start": v(-109.05, 80) * mm, "end": v(-109.05, 76) * mm});
            skLineSegment(sketch, "E206", {"start": v(-109.05, 76) * mm, "end": v(-110.15, 76) * mm});
            skLineSegment(sketch, "E207", {"start": v(-110.15, 76) * mm, "end": v(-110.15, 74) * mm});
            skLineSegment(sketch, "E208", {"start": v(-110.15, 74) * mm, "end": v(-109.05, 74) * mm});
            skLineSegment(sketch, "E209", {"start": v(-109.05, 74) * mm, "end": v(-109.05, 70.76) * mm});
            skLineSegment(sketch, "E210", {"start": v(-109.05, 70.76) * mm, "end": v(-107.95, 70.76) * mm});
            skLineSegment(sketch, "E211.MirrorCS", {"start": v(-106.85, 80) * mm, "end": v(-106.85, 76) * mm});
            skLineSegment(sketch, "E212.MirrorCS", {"start": v(-106.85, 76) * mm, "end": v(-105.75, 76) * mm});
            skLineSegment(sketch, "E213.MirrorCS", {"start": v(-105.75, 76) * mm, "end": v(-105.75, 74) * mm});
            skLineSegment(sketch, "E214.MirrorCS", {"start": v(-105.75, 74) * mm, "end": v(-106.85, 74) * mm});
            skLineSegment(sketch, "E215.MirrorCS", {"start": v(-106.85, 74) * mm, "end": v(-106.85, 70.76) * mm});
            skLineSegment(sketch, "E216.MirrorCS", {"start": v(-106.85, 70.76) * mm, "end": v(-107.95, 70.76) * mm});
            skLineSegment(sketch, "E217", {"start": v(-109.05, 80) * mm, "end": v(-106.85, 80) * mm});
            skSolve(sketch);
        }
        {
            var Q0;
            Q0 = qSketchRegion(id + "F16", true);
            extrude(context, id + "F17", {"entities" : qUnion([Q0]), "operationType" : NewBodyOperationType.REMOVE, "oppositeDirection" : true, "depth" : 25.4 * mm});
        }
    });
